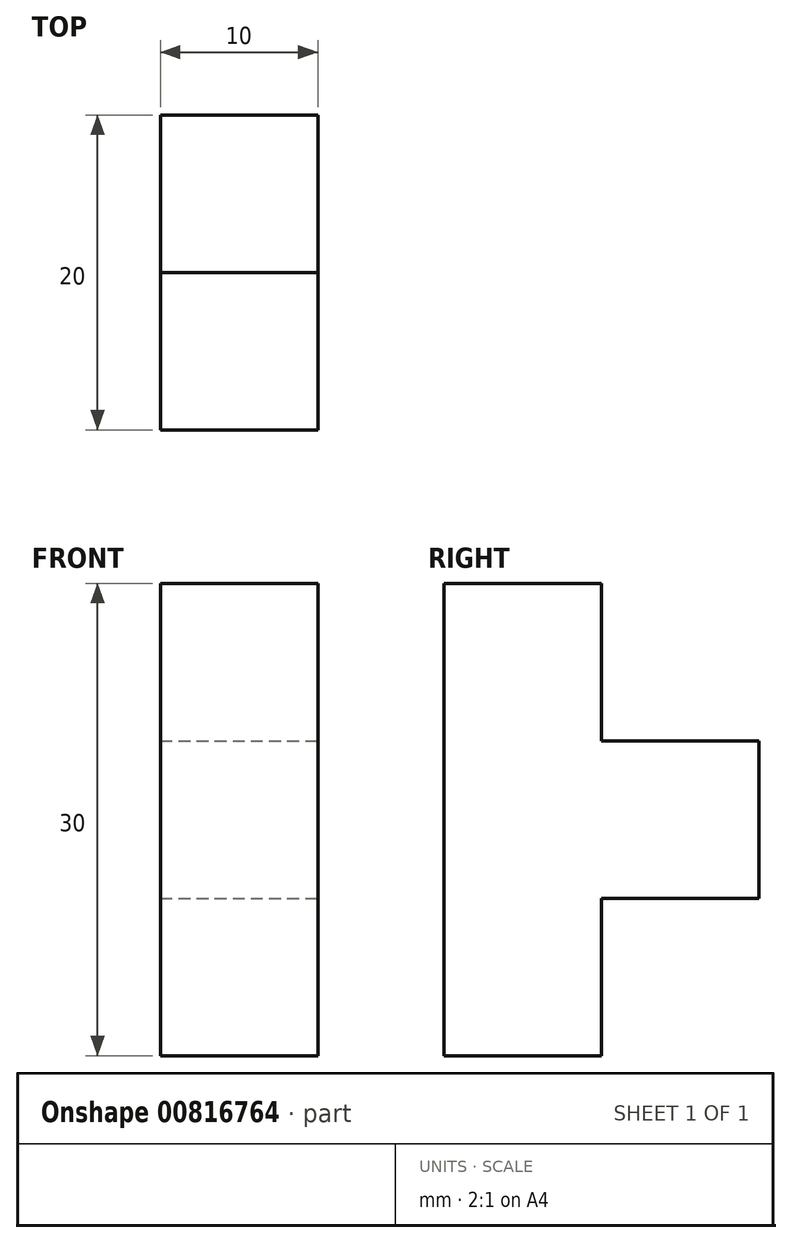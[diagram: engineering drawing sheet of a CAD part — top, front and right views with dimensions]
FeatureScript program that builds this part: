
annotation { "Feature Type Name" : "Feature", "Feature Type Description" : "" }
export const myFeature = defineFeature(function(context is Context, id is Id, definition is map)
    precondition{}
    {
        {
            var Q0;
            Q0=qCreatedBy(makeId("Top.planeOp"),FACE);
            var sketch = newSketch(context, id + "F0", { "sketchPlane" : qUnion([Q0])});
            skLineSegment(sketch, "E0.bottom", {"start": v(0, 0) * mm, "end": v(10, 0) * mm});
            skLineSegment(sketch, "E0.top", {"start": v(0, 10) * mm, "end": v(10, 10) * mm});
            skLineSegment(sketch, "E0.left", {"start": v(0, 0) * mm, "end": v(0, 10) * mm});
            skLineSegment(sketch, "E0.right", {"start": v(10, 0) * mm, "end": v(10, 10) * mm});
            skSolve(sketch);
        }
        {
            var Q0;
            Q0=makeQuery(id+"F0.imprint","IMPRINT",FACE,{"disambiguationData":[TD([[makeQuery(id+"F0.imprint","IMPRINT",EDGE,{"derivedFrom":sQuery(id+"F0.wireOp",EDGE,"E0.bottom")}),1.0]])]});
            extrude(context, id + "F1", {"entities" : qUnion([Q0]), "depth" : 10 * mm, "offsetDistance" : 25 * mm});
        }
        {
            var Q0;
            Q0=makeQuery(id+"F1.opExtrude","CAP_FACE",FACE,{"disambiguationData":[OSD([sQuery(id+"F0.wireOp",EDGE,"E0.bottom"),sQuery(id+"F0.wireOp",EDGE,"E0.top"),sQuery(id+"F0.wireOp",EDGE,"E0.left"),sQuery(id+"F0.wireOp",EDGE,"E0.right")])],"isStart":false});
            extrude(context, id + "F2", {"entities" : qUnion([Q0]), "operationType" : NewBodyOperationType.ADD, "depth" : 20 * mm, "offsetDistance" : 25 * mm});
        }
        {
            var Q0;
            {var subQ0=sQuery(id+"F0.wireOp",EDGE,"E0.top");Q0=makeQuery(id+"F2.boolean.opBoolean","MERGE",FACE,{"derivedFrom":[makeQuery(id+"F1.opExtrude","SWEPT_FACE",FACE,{"disambiguationData":[OSD([subQ0])]}),makeQuery(id+"F2.opExtrude","SWEPT_FACE",FACE,{"disambiguationData":[OSD([subQ0])]})]});}
            var sketch = newSketch(context, id + "F3", { "sketchPlane" : qUnion([Q0])});
            skLineSegment(sketch, "E1.bottom", {"start": v(0, 20) * mm, "end": v(-10, 20) * mm});
            skLineSegment(sketch, "E1.top", {"start": v(0, 10) * mm, "end": v(-10, 10) * mm});
            skLineSegment(sketch, "E1.left", {"start": v(0, 20) * mm, "end": v(0, 10) * mm});
            skLineSegment(sketch, "E1.right", {"start": v(-10, 20) * mm, "end": v(-10, 10) * mm});
            skSolve(sketch);
        }
        {
            var Q0;
            Q0=makeQuery(id+"F3.imprint","IMPRINT",FACE,{"disambiguationData":[TD([[makeQuery(id+"F3.imprint","IMPRINT",EDGE,{"derivedFrom":sQuery(id+"F3.wireOp",EDGE,"E1.bottom")}),1.0]])]});
            extrude(context, id + "F4", {"entities" : qUnion([Q0]), "operationType" : NewBodyOperationType.ADD, "depth" : 10 * mm, "offsetDistance" : 25 * mm});
        }
    });
